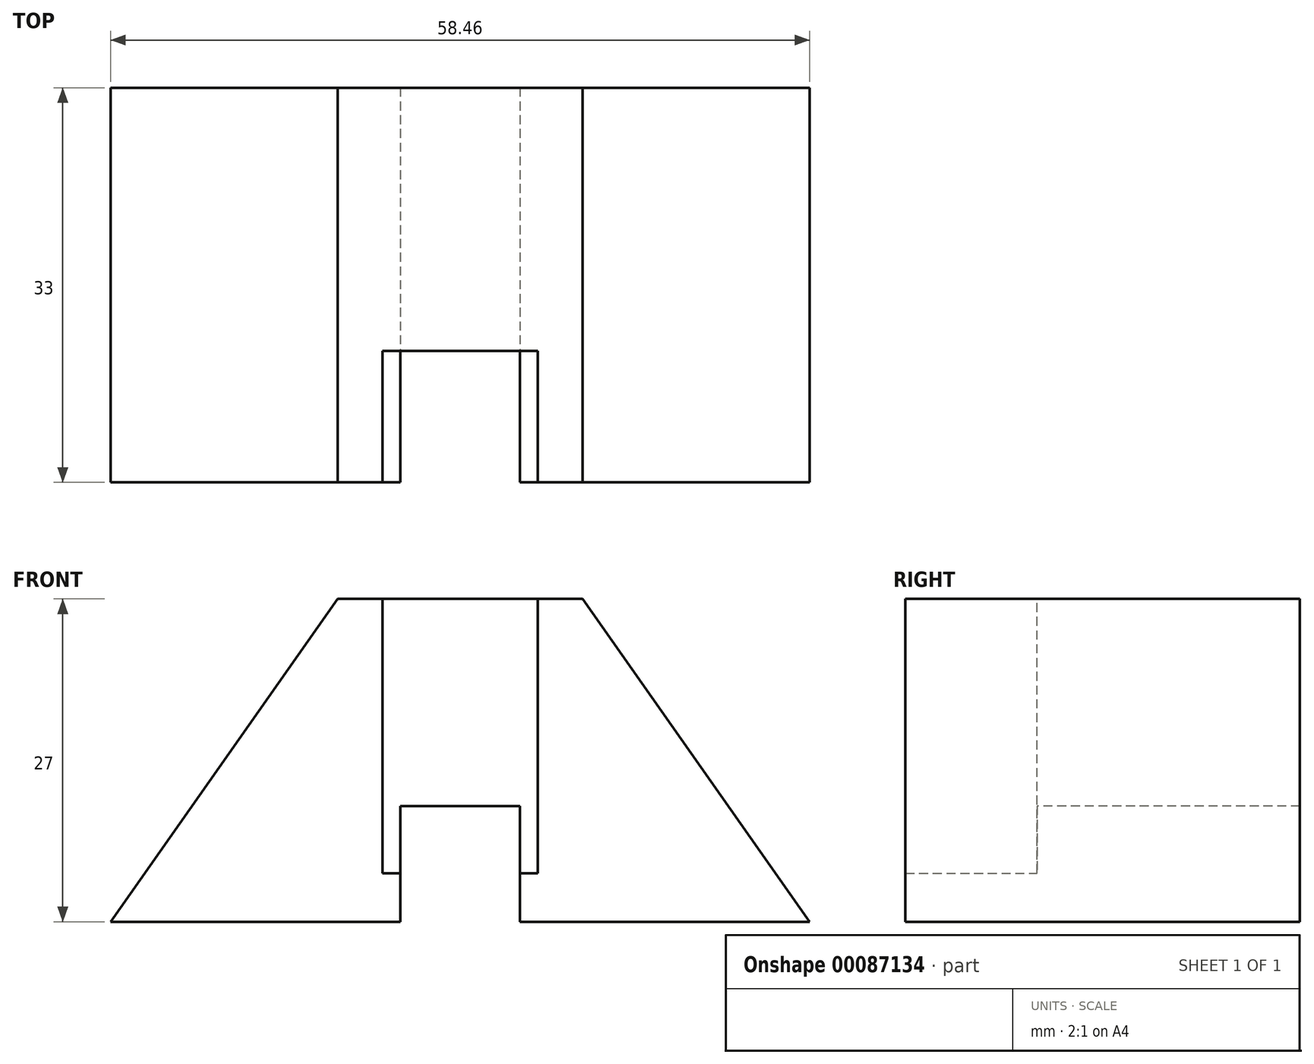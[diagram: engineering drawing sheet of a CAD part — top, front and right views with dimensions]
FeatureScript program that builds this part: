
annotation { "Feature Type Name" : "Feature", "Feature Type Description" : "" }
export const myFeature = defineFeature(function(context is Context, id is Id, definition is map)
    precondition{}
    {
        {
            var Q0;
            Q0=qCreatedBy(makeId("Front.planeOp"),FACE);
            var sketch = newSketch(context, id + "F0", { "sketchPlane" : qUnion([Q0])});
            skLineSegment(sketch, "E0", {"start": v(-10.25, 27) * mm, "end": v(-29.23, 0) * mm});
            skLineSegment(sketch, "E1", {"start": v(-29.23, 0) * mm, "end": v(29.23, 0) * mm});
            skLineSegment(sketch, "E2", {"start": v(29.23, 0) * mm, "end": v(10.25, 27) * mm});
            skLineSegment(sketch, "E3", {"start": v(10.25, 27) * mm, "end": v(-10.25, 27) * mm});
            skSolve(sketch);
        }
        {
            var Q0;
            Q0 = qSketchRegion(id + "F0", true);
            extrude(context, id + "F1", {"entities" : qUnion([Q0]), "depth" : 33 * mm});
        }
        {
            var Q0;
            Q0=makeQuery(id+"F1.opExtrude","CAP_FACE",FACE,{"disambiguationData":[OSD([sQuery(id+"F0.wireOp",EDGE,"E0"),sQuery(id+"F0.wireOp",EDGE,"E1"),sQuery(id+"F0.wireOp",EDGE,"E2"),sQuery(id+"F0.wireOp",EDGE,"E3")])],"isStart":false});
            var sketch = newSketch(context, id + "F2", { "sketchPlane" : qUnion([Q0])});
            skLineSegment(sketch, "E4.bottom", {"start": v(-5, 0) * mm, "end": v(5, 0) * mm});
            skLineSegment(sketch, "E4.top", {"start": v(-5, 9.68) * mm, "end": v(5, 9.68) * mm});
            skLineSegment(sketch, "E4.left", {"start": v(-5, 0) * mm, "end": v(-5, 9.68) * mm});
            skLineSegment(sketch, "E4.right", {"start": v(5, 0) * mm, "end": v(5, 9.68) * mm});
            skSolve(sketch);
        }
        {
            var Q0;
            Q0 = qSketchRegion(id + "F2", true);
            extrude(context, id + "F3", {"entities" : qUnion([Q0]), "operationType" : NewBodyOperationType.REMOVE, "oppositeDirection" : true, "depth" : 33 * mm});
        }
        {
            var Q0;
            Q0=makeQuery(id+"F1.opExtrude","CAP_FACE",FACE,{"disambiguationData":[OSD([sQuery(id+"F0.wireOp",EDGE,"E0"),sQuery(id+"F0.wireOp",EDGE,"E1"),sQuery(id+"F0.wireOp",EDGE,"E2"),sQuery(id+"F0.wireOp",EDGE,"E3")])],"isStart":false});
            var sketch = newSketch(context, id + "F4", { "sketchPlane" : qUnion([Q0])});
            skLineSegment(sketch, "E5.bottom", {"start": v(-6.5, 4.05) * mm, "end": v(6.5, 4.05) * mm});
            skLineSegment(sketch, "E5.top", {"start": v(-6.5, 27) * mm, "end": v(6.5, 27) * mm});
            skLineSegment(sketch, "E5.left", {"start": v(-6.5, 4.05) * mm, "end": v(-6.5, 27) * mm});
            skLineSegment(sketch, "E5.right", {"start": v(6.5, 4.05) * mm, "end": v(6.5, 27) * mm});
            skSolve(sketch);
        }
        {
            var Q0;
            Q0 = qSketchRegion(id + "F4", true);
            extrude(context, id + "F5", {"entities" : qUnion([Q0]), "operationType" : NewBodyOperationType.REMOVE, "oppositeDirection" : true, "depth" : 11 * mm});
        }
    });
